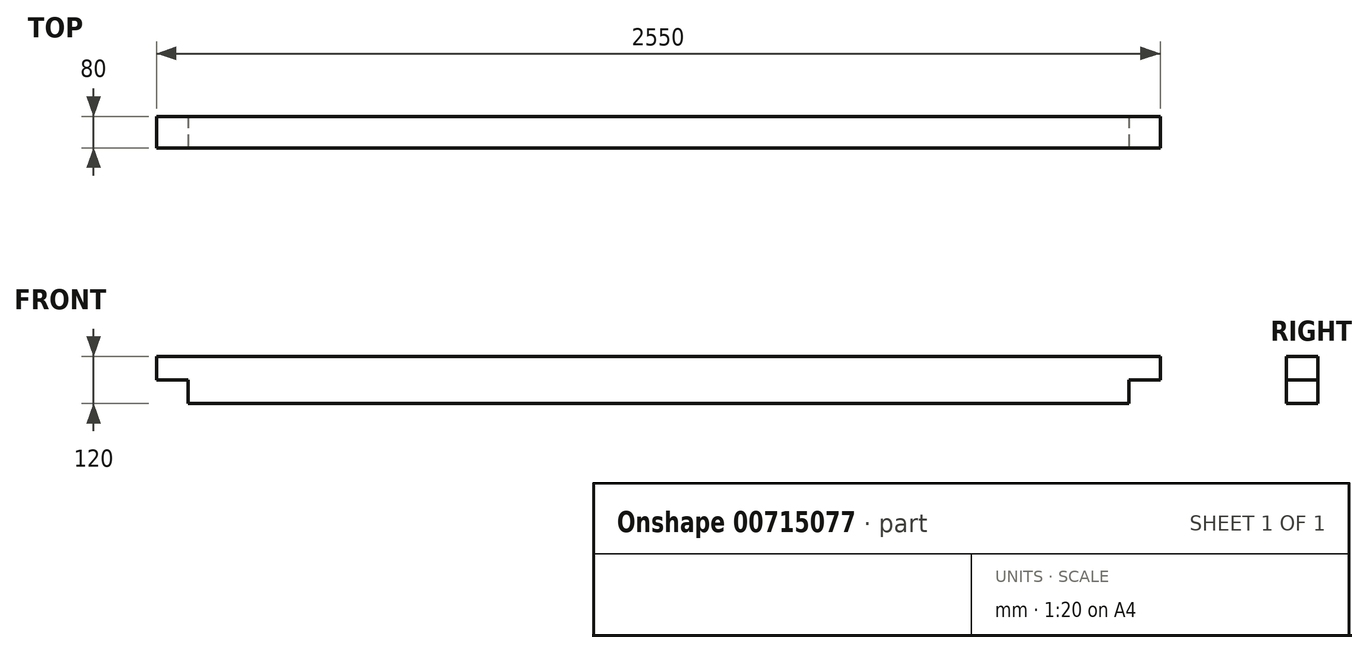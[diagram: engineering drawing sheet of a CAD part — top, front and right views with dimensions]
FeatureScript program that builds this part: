
annotation { "Feature Type Name" : "Feature", "Feature Type Description" : "" }
export const myFeature = defineFeature(function(context is Context, id is Id, definition is map)
    precondition{}
    {
        {
            var Q0;
            Q0=qCreatedBy(makeId("Right.planeOp"),FACE);
            var sketch = newSketch(context, id + "F0", { "sketchPlane" : qUnion([Q0])});
            skLineSegment(sketch, "E0.bottom", {"start": v(-40, 60) * mm, "end": v(40, 60) * mm});
            skLineSegment(sketch, "E0.top", {"start": v(-40, -60) * mm, "end": v(40, -60) * mm});
            skLineSegment(sketch, "E0.left", {"start": v(-40, 60) * mm, "end": v(-40, -60) * mm});
            skLineSegment(sketch, "E0.right", {"start": v(40, 60) * mm, "end": v(40, -60) * mm});
            skPoint(sketch, "E0.middle", {"position": v(0, 0) * mm});
            skSolve(sketch);
        }
        {
            var Q0;
            Q0=makeQuery(id+"F0.imprint","IMPRINT",FACE,{"disambiguationData":[TD([[makeQuery(id+"F0.imprint","IMPRINT",EDGE,{"derivedFrom":sQuery(id+"F0.wireOp",EDGE,"E0.bottom")}),-1.0]])]});
            extrude(context, id + "F1", {"entities" : qUnion([Q0]), "depth" : 2550 * mm, "offsetDistance" : 25 * mm});
        }
        {
            var Q0;
            Q0=makeQuery(id+"F1.opExtrude","SWEPT_FACE",FACE,{"disambiguationData":[OSD([sQuery(id+"F0.wireOp",EDGE,"E0.left")])]});
            var sketch = newSketch(context, id + "F2", { "sketchPlane" : qUnion([Q0])});
            skLineSegment(sketch, "E1.bottom", {"start": v(-80, 0) * mm, "end": v(80, 0) * mm});
            skLineSegment(sketch, "E1.top", {"start": v(-80, -120) * mm, "end": v(80, -120) * mm});
            skLineSegment(sketch, "E1.left", {"start": v(-80, 0) * mm, "end": v(-80, -120) * mm});
            skLineSegment(sketch, "E1.right", {"start": v(80, 0) * mm, "end": v(80, -120) * mm});
            skPoint(sketch, "E1.middle", {"position": v(0, -60) * mm});
            skPoint(sketch, "E1.cornerSnap0", {"position": v(0, 0) * mm});
            skLineSegment(sketch, "E2.bottom", {"start": v(2630, 0) * mm, "end": v(2470, 0) * mm});
            skLineSegment(sketch, "E2.top", {"start": v(2630, -120) * mm, "end": v(2470, -120) * mm});
            skLineSegment(sketch, "E2.left", {"start": v(2630, 0) * mm, "end": v(2630, -120) * mm});
            skLineSegment(sketch, "E2.right", {"start": v(2470, 0) * mm, "end": v(2470, -120) * mm});
            skPoint(sketch, "E2.middle", {"position": v(2550, -60) * mm});
            skPoint(sketch, "E2.cornerSnap0", {"position": v(2550, 0) * mm});
            skSolve(sketch);
        }
        {
            var Q0;
            {var subQ0=sQuery(id+"F2.wireOp",EDGE,"E2.right");var subQ1=sQuery(id+"F2.wireOp",EDGE,"E2.bottom");var subQ2=makeQuery(id+"F2.imprint","INTERSECT",VERTEX,{"derivedFrom":[subQ1,subQ0]});Q0=makeQuery(id+"F2.imprint","IMPRINT",FACE,{"disambiguationData":[TD([[makeQuery(id+"F2.imprint","IMPRINT",EDGE,{"disambiguationData":[TD([[subQ2,1.0]])],"derivedFrom":subQ1}),1.0]])]});}
            var Q1;
            {var subQ0=sQuery(id+"F2.wireOp",EDGE,"E1.right");var subQ1=sQuery(id+"F2.wireOp",EDGE,"E1.bottom");var subQ2=makeQuery(id+"F2.imprint","INTERSECT",VERTEX,{"derivedFrom":[subQ1,subQ0]});Q1=makeQuery(id+"F2.imprint","IMPRINT",FACE,{"disambiguationData":[TD([[makeQuery(id+"F2.imprint","IMPRINT",EDGE,{"disambiguationData":[TD([[subQ2,1.0]])],"derivedFrom":subQ1}),-1.0]])]});}
            extrude(context, id + "F3", {"entities" : qUnion([Q0, Q1]), "operationType" : NewBodyOperationType.REMOVE, "endBound" : BoundingType.UP_TO_NEXT, "oppositeDirection" : true, "depth" : 25 * mm, "offsetDistance" : 25 * mm});
        }
    });
